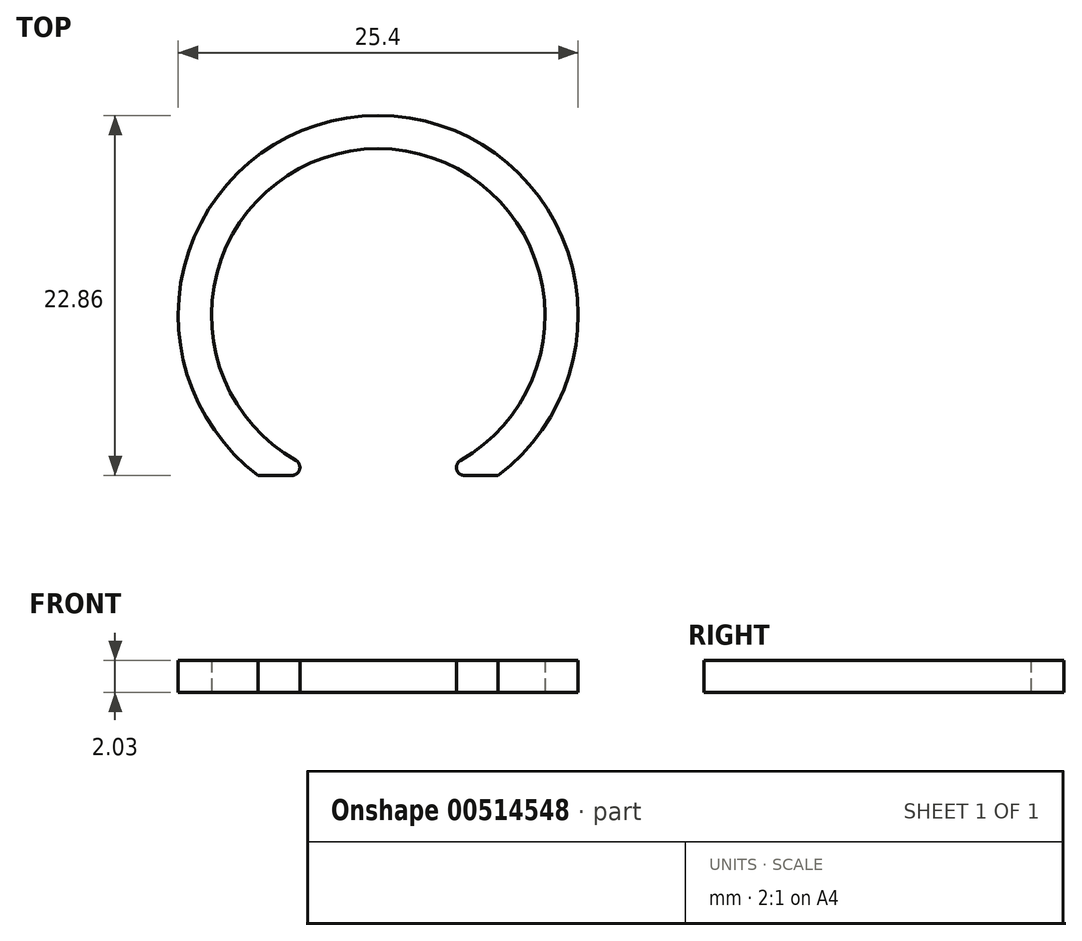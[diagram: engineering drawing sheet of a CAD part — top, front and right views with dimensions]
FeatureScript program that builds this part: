
annotation { "Feature Type Name" : "Feature", "Feature Type Description" : "" }
export const myFeature = defineFeature(function(context is Context, id is Id, definition is map)
    precondition{}
    {
        {
            var Q0;
            Q0=qCreatedBy(makeId("Top.planeOp"),FACE);
            var sketch = newSketch(context, id + "F0", { "sketchPlane" : qUnion([Q0])});
            skArc(sketch, "E0", {"start": v(3, -10.16) * mm, "mid": v(0, 10.6) * mm, "end": v(-3, -10.16) * mm});
            skArc(sketch, "E1", {"start": v(7.62, -10.16) * mm, "mid": v(0, 12.7) * mm, "end": v(-7.62, -10.16) * mm});
            skLineSegment(sketch, "E2", {"start": v(-7.62, -10.16) * mm, "end": v(-3, -10.16) * mm});
            skLineSegment(sketch, "E3.trimOffspring", {"start": v(3, -10.16) * mm, "end": v(7.62, -10.16) * mm});
            skSolve(sketch);
        }
        {
            var Q0;
            Q0 = qSketchRegion(id + "F0", true);
            extrude(context, id + "F1", {"entities" : qUnion([Q0]), "depth" : 2.03 * mm});
        }
        {
            var Q0;
            Q0=makeQuery(id+"F1.opExtrude","SWEPT_EDGE",EDGE,{"disambiguationData":[OSD([sQuery(id+"F0.wireOp",EDGE,"E0"),sQuery(id+"F0.wireOp",EDGE,"E2")])]});
            var Q1;
            Q1=makeQuery(id+"F1.opExtrude","SWEPT_EDGE",EDGE,{"disambiguationData":[OSD([sQuery(id+"F0.wireOp",EDGE,"E0"),sQuery(id+"F0.wireOp",EDGE,"E3.trimOffspring")])]});
            fillet(context, id + "F2", {"entities" : qUnion([Q0, Q1]), "radius" : 0.5 * mm, "tangentPropagation" : true, "allowEdgeOverflow" : false});
        }
    });
